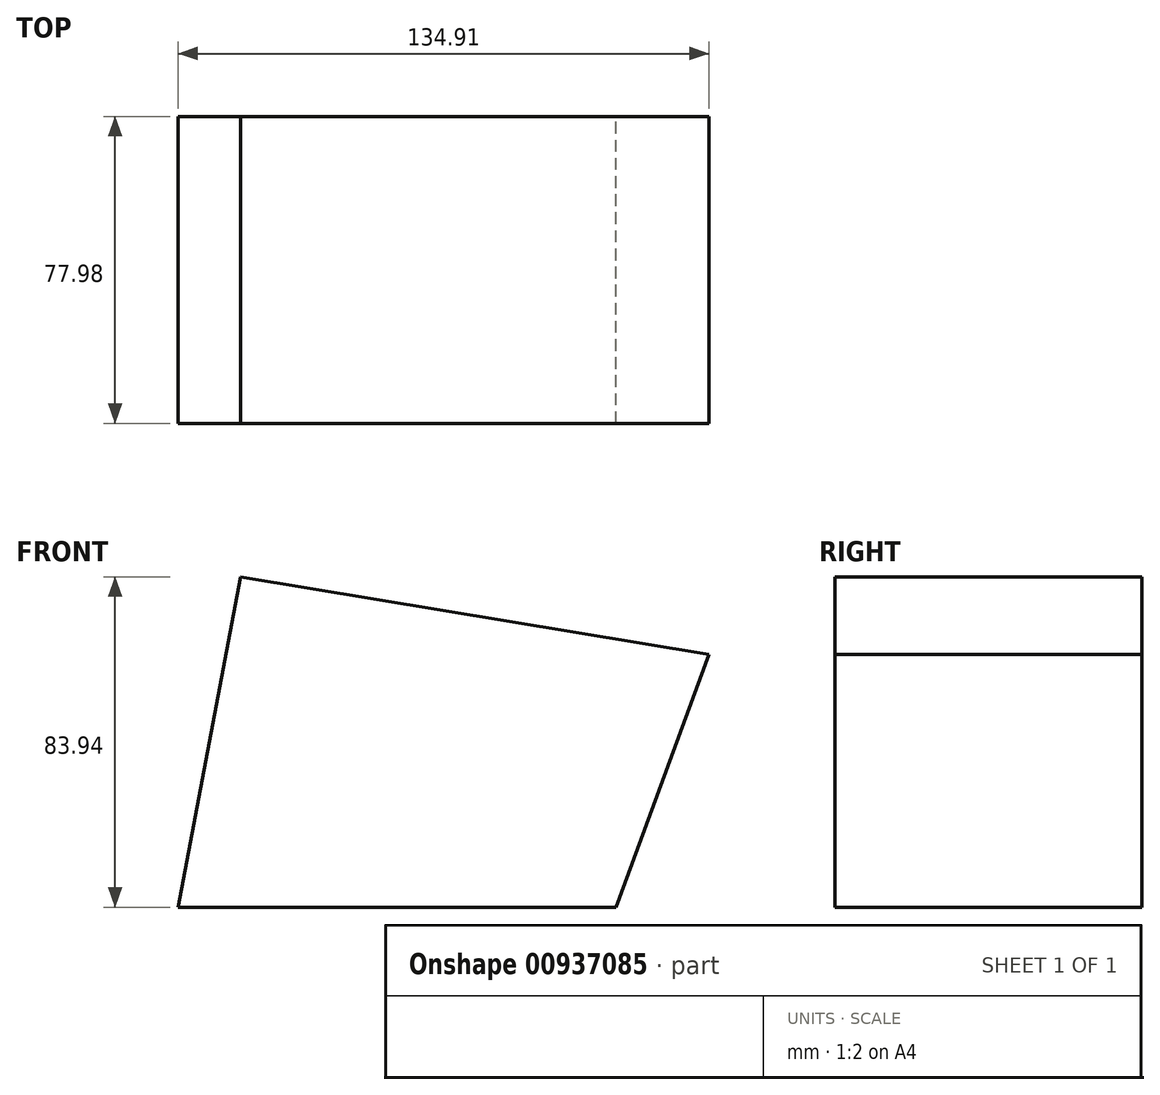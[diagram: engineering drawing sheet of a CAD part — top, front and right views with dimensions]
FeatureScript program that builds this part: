
annotation { "Feature Type Name" : "Feature", "Feature Type Description" : "" }
export const myFeature = defineFeature(function(context is Context, id is Id, definition is map)
    precondition{}
    {
        {
            var Q0;
            Q0=qCreatedBy(makeId("Front.planeOp"),FACE);
            var sketch = newSketch(context, id + "F0", { "sketchPlane" : qUnion([Q0])});
            skLineSegment(sketch, "E0", {"start": v(-94.96, 54.05) * mm, "end": v(24.14, 34.33) * mm});
            skLineSegment(sketch, "E1", {"start": v(24.14, 34.33) * mm, "end": v(0.47, -29.9) * mm});
            skLineSegment(sketch, "E2", {"start": v(0.47, -29.9) * mm, "end": v(-110.77, -29.9) * mm});
            skLineSegment(sketch, "E3", {"start": v(-110.77, -29.9) * mm, "end": v(-94.96, 54.05) * mm});
            skSolve(sketch);
        }
        {
            var Q0;
            Q0 = qSketchRegion(id + "F0", true);
            var Q1;
            Q1=makeQuery(id+"F0.imprint","IMPRINT",FACE,{"disambiguationData":[TD([[makeQuery(id+"F0.imprint","IMPRINT",EDGE,{"derivedFrom":sQuery(id+"F0.wireOp",EDGE,"E0")}),-1.0]])]});
            extrude(context, id + "F1", {"entities" : qUnion([Q0, Q1]), "depth" : 77.98 * mm, "offsetDistance" : 25.4 * mm});
        }
    });
